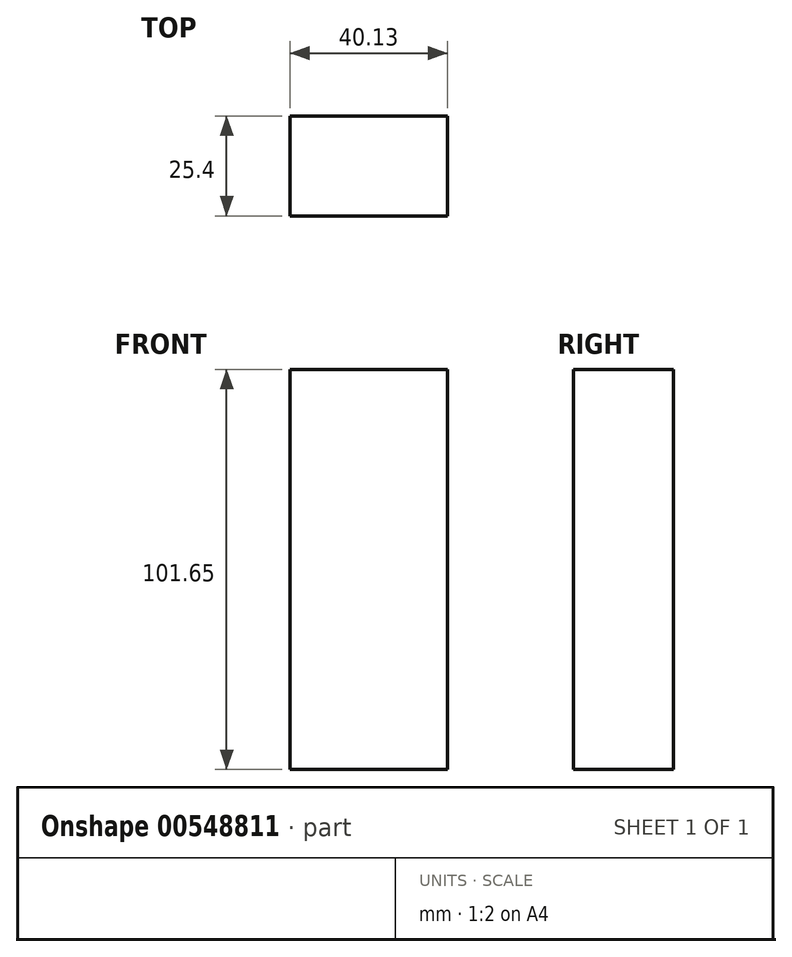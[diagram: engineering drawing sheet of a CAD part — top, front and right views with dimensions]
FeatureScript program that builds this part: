
annotation { "Feature Type Name" : "Feature", "Feature Type Description" : "" }
export const myFeature = defineFeature(function(context is Context, id is Id, definition is map)
    precondition{}
    {
        {
            var Q0;
            Q0=qCreatedBy(makeId("Front.planeOp"),FACE);
            var sketch = newSketch(context, id + "F0", { "sketchPlane" : qUnion([Q0])});
            skLineSegment(sketch, "E0.bottom", {"start": v(-65.1, -18.28) * mm, "end": v(65.1, -18.28) * mm});
            skLineSegment(sketch, "E0.top", {"start": v(-65.1, 18.28) * mm, "end": v(65.1, 18.28) * mm});
            skLineSegment(sketch, "E0.left", {"start": v(-65.1, -18.28) * mm, "end": v(-65.1, 18.28) * mm});
            skLineSegment(sketch, "E0.right", {"start": v(65.1, -18.28) * mm, "end": v(65.1, 18.28) * mm});
            skPoint(sketch, "E0.middle", {"position": v(0, 0) * mm});
            skLineSegment(sketch, "E1.bottom", {"start": v(102.98, 20.95) * mm, "end": v(143.1, 20.95) * mm});
            skLineSegment(sketch, "E1.top", {"start": v(102.98, 122.6) * mm, "end": v(143.1, 122.6) * mm});
            skLineSegment(sketch, "E1.left", {"start": v(102.98, 20.95) * mm, "end": v(102.98, 122.6) * mm});
            skLineSegment(sketch, "E1.right", {"start": v(143.1, 20.95) * mm, "end": v(143.1, 122.6) * mm});
            skPoint(sketch, "E1.middle", {"position": v(123.05, 71.78) * mm});
            skSolve(sketch);
        }
        {
            var Q0;
            Q0=makeQuery(id+"F0.imprint","IMPRINT",FACE,{"disambiguationData":[TD([[makeQuery(id+"F0.imprint","IMPRINT",EDGE,{"derivedFrom":sQuery(id+"F0.wireOp",EDGE,"E1.bottom")}),1.0]])]});
            extrude(context, id + "F1", {"entities" : qUnion([Q0]), "depth" : 25.4 * mm, "offsetDistance" : 25.4 * mm});
        }
    });
